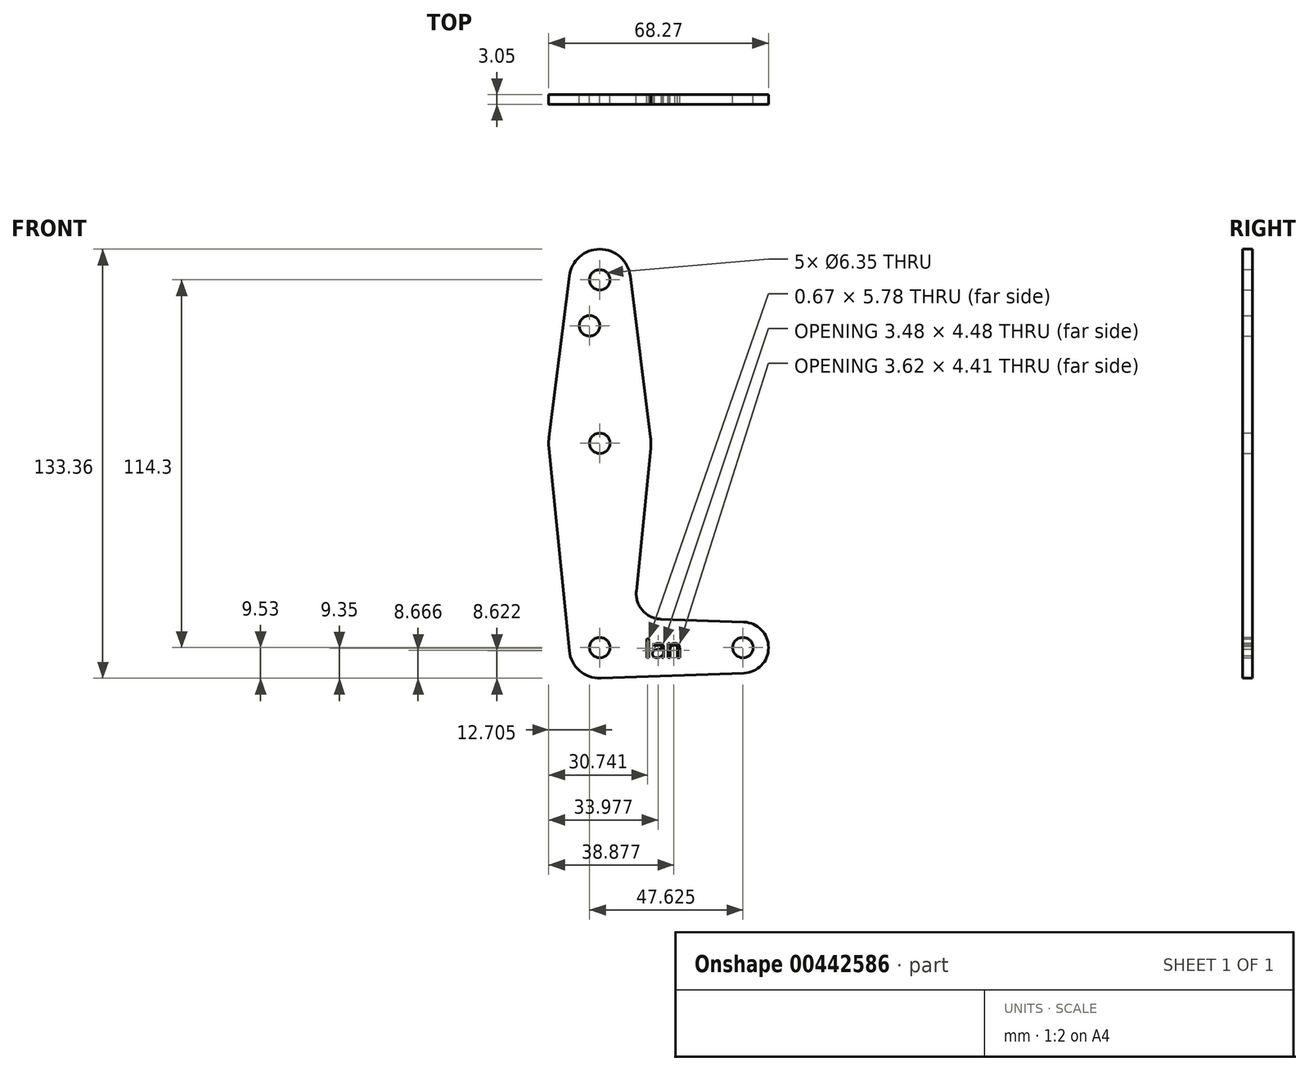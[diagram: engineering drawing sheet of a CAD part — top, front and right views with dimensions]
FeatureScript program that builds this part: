
annotation { "Feature Type Name" : "Feature", "Feature Type Description" : "" }
export const myFeature = defineFeature(function(context is Context, id is Id, definition is map)
    precondition{}
    {
        {
            var Q0;
            Q0=qCreatedBy(makeId("Front.planeOp"),FACE);
            var sketch = newSketch(context, id + "F0", { "sketchPlane" : qUnion([Q0])});
            skLineSegment(sketch, "E0", {"start": v(0, 0) * mm, "end": v(44.45, 0) * mm, "construction": true});
            skLineSegment(sketch, "E1", {"start": v(0, 0) * mm, "end": v(0, 114.3) * mm, "construction": true});
            skCircle(sketch, "E2", {"center": v(0, 0) * mm, "radius": 9.53 * mm});
            skCircle(sketch, "E3", {"center": v(44.45, 0) * mm, "radius": 7.94 * mm});
            skCircle(sketch, "E4", {"center": v(0, 114.3) * mm, "radius": 9.53 * mm});
            skCircle(sketch, "E5", {"center": v(0, 63.5) * mm, "radius": 15.88 * mm});
            skLineSegment(sketch, "E6", {"start": v(9.45, 115.5) * mm, "end": v(15.75, 65.48) * mm});
            skLineSegment(sketch, "E7", {"start": v(-15.75, 65.48) * mm, "end": v(-9.45, 115.5) * mm});
            skLineSegment(sketch, "E8", {"start": v(-15.8, 61.91) * mm, "end": v(-9.48, -0.95) * mm});
            skLineSegment(sketch, "E9", {"start": v(15.8, 61.91) * mm, "end": v(11.34, 17.6) * mm});
            skLineSegment(sketch, "E10", {"start": v(18.97, 8.85) * mm, "end": v(44.73, 7.93) * mm});
            skLineSegment(sketch, "E11", {"start": v(0.34, -9.52) * mm, "end": v(44.73, -7.93) * mm});
            skCircle(sketch, "E12", {"center": v(0, 114.3) * mm, "radius": 3.18 * mm});
            skCircle(sketch, "E13", {"center": v(0, 63.5) * mm, "radius": 3.18 * mm});
            skCircle(sketch, "E14", {"center": v(0, 0) * mm, "radius": 3.18 * mm});
            skCircle(sketch, "E15", {"center": v(44.45, 0) * mm, "radius": 3.18 * mm});
            skCircle(sketch, "E16", {"center": v(-3.18, 100.03) * mm, "radius": 3.18 * mm});
            skPoint(sketch, "E17.newPointA", {"position": v(9.48, -0.95) * mm});
            skArc(sketch, "E17.filletArc", {"start": v(11.34, 17.6) * mm, "mid": v(13.26, 11.57) * mm, "end": v(18.97, 8.85) * mm});
            skText(sketch, "E18", { "text": "Ian", "fontName": "OpenSans-Regular.ttf"});
            const initialGuessF0  = {"E18": [0.01373, -0.00307, 1, 0, 0.00583]};
            skSetInitialGuess(sketch, initialGuessF0);
            skSolve(sketch);
        }
        {
            var Q0;
            Q0 = qSketchRegion(id + "F0", true);
            extrude(context, id + "F1", {"entities" : qUnion([Q0]), "depth" : 3.05 * mm});
        }
    });
